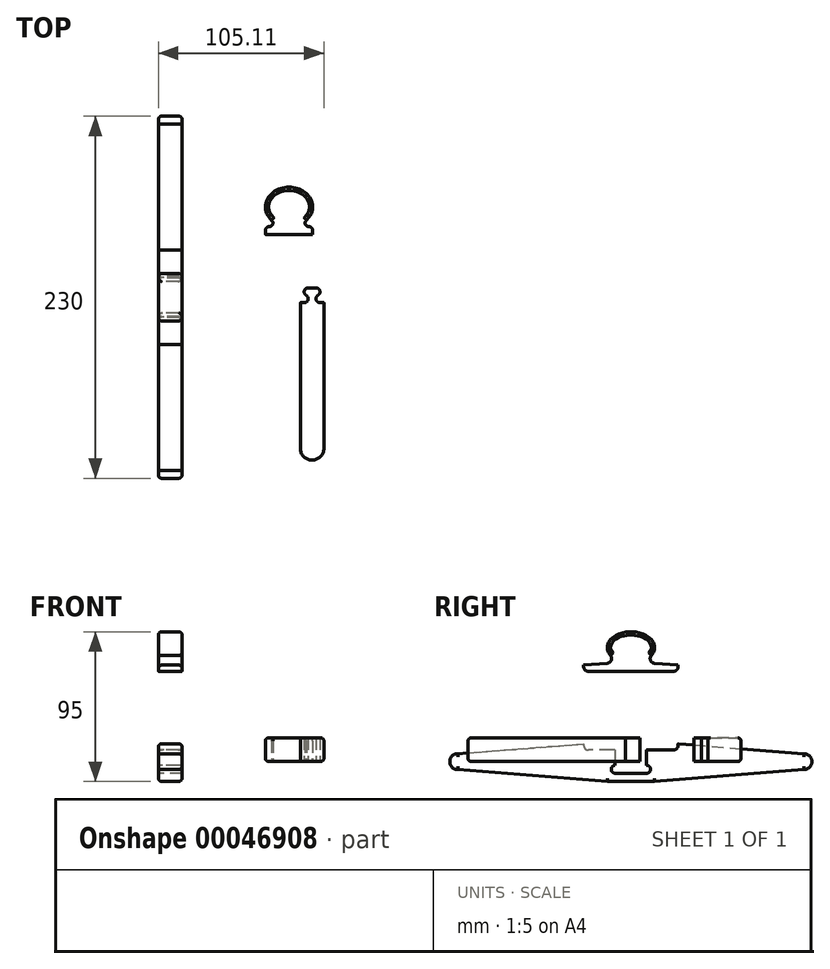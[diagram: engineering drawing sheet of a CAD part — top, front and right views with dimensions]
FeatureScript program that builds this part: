
annotation { "Feature Type Name" : "Feature", "Feature Type Description" : "" }
export const myFeature = defineFeature(function(context is Context, id is Id, definition is map)
    precondition{}
    {
        {
            var Q0;
            Q0=qCreatedBy(makeId("Right.planeOp"),FACE);
            var sketch = newSketch(context, id + "F0", { "sketchPlane" : qUnion([Q0])});
            skLineSegment(sketch, "E0.MirrorCS", {"start": v(-14.97, 12.4) * mm, "end": v(-109.97, 4.9) * mm, "construction": true});
            skLineSegment(sketch, "E1.rect.top", {"start": v(-9.97, -7.45) * mm, "end": v(10.03, -7.45) * mm});
            skLineSegment(sketch, "E2.rect.top", {"start": v(-14.97, -12.6) * mm, "end": v(15.03, -12.6) * mm});
            skLineSegment(sketch, "E1.rect.bottom", {"start": v(-9.97, 7.26) * mm, "end": v(10.03, 7.26) * mm});
            skLineSegment(sketch, "E3", {"start": v(0.03, 22.4) * mm, "end": v(-14.97, 22.4) * mm, "construction": true});
            skLineSegment(sketch, "E2.rect.right", {"start": v(15.03, 12.4) * mm, "end": v(15.03, -12.6) * mm, "construction": true});
            skLineSegment(sketch, "E1.rect.left", {"start": v(-9.97, 7.26) * mm, "end": v(-9.97, -2.45) * mm});
            skLineSegment(sketch, "E2.rect.left", {"start": v(-14.97, 12.4) * mm, "end": v(-14.97, -12.6) * mm, "construction": true});
            skLineSegment(sketch, "E4", {"start": v(15.03, -0.1) * mm, "end": v(115.03, -0.1) * mm, "construction": true});
            skLineSegment(sketch, "E5.MirrorCS", {"start": v(-14.97, -12.6) * mm, "end": v(-109.97, -5.1) * mm});
            skPoint(sketch, "E4.endSnap0", {"position": v(15.03, -0.1) * mm});
            skLineSegment(sketch, "E6.MirrorCS", {"start": v(15.03, 12.4) * mm, "end": v(110.03, 4.9) * mm, "construction": true});
            skLineSegment(sketch, "E7", {"start": v(15.03, -12.6) * mm, "end": v(110.03, -5.1) * mm});
            skEllipse(sketch, "E8", {"center": v(0.03, 22.4) * mm, "majorRadius": 10 * mm, "minorRadius": 15 * mm, "majorAxis": v(0, 1)});
            skLineSegment(sketch, "E1.rect.right", {"start": v(10.03, 7.26) * mm, "end": v(10.03, -2.45) * mm});
            skLineSegment(sketch, "E9", {"start": v(0.03, 12.4) * mm, "end": v(0.03, 32.4) * mm, "construction": true});
            skLineSegment(sketch, "E10", {"start": v(0.03, 12.4) * mm, "end": v(0.03, -12.6) * mm, "construction": true});
            skArc(sketch, "E11.MirrorCS", {"start": v(-114.97, -0.1) * mm, "mid": v(-113.5, 3.44) * mm, "end": v(-109.97, 4.9) * mm});
            skArc(sketch, "E12.MirrorCS", {"start": v(-114.97, -0.1) * mm, "mid": v(-113.5, -3.63) * mm, "end": v(-109.97, -5.1) * mm});
            skArc(sketch, "E13", {"start": v(115.03, -0.1) * mm, "mid": v(113.56, 3.44) * mm, "end": v(110.03, 4.9) * mm});
            skArc(sketch, "E14.MirrorCS", {"start": v(115.03, -0.1) * mm, "mid": v(113.56, -3.63) * mm, "end": v(110.03, -5.1) * mm});
            skLineSegment(sketch, "E15", {"start": v(115.03, -0.1) * mm, "end": v(110.03, -0.1) * mm, "construction": true});
            skLineSegment(sketch, "E16", {"start": v(30.03, 10.26) * mm, "end": v(30.03, 11.22) * mm, "construction": true});
            skLineSegment(sketch, "E17", {"start": v(0.03, 7.26) * mm, "end": v(27.03, 7.26) * mm, "construction": true});
            skArc(sketch, "E18.filletArc", {"start": v(27.03, 7.26) * mm, "mid": v(29.15, 8.14) * mm, "end": v(30.03, 10.26) * mm, "construction": true});
            skLineSegment(sketch, "E19", {"start": v(0.03, 7.26) * mm, "end": v(27.03, 7.26) * mm});
            skLineSegment(sketch, "E20", {"start": v(30.03, 10.26) * mm, "end": v(30.03, 11.22) * mm});
            skLineSegment(sketch, "E21", {"start": v(30.03, 11.22) * mm, "end": v(15.03, 12.4) * mm});
            skLineSegment(sketch, "E22", {"start": v(30.03, 11.22) * mm, "end": v(110.03, 4.9) * mm});
            skLineSegment(sketch, "E23.MirrorCS", {"start": v(0.03, 7.26) * mm, "end": v(-26.97, 7.26) * mm});
            skArc(sketch, "E24.MirrorCS", {"start": v(-26.97, 7.26) * mm, "mid": v(-29.1, 8.14) * mm, "end": v(-29.97, 10.26) * mm});
            skLineSegment(sketch, "E25.MirrorCS", {"start": v(-29.97, 10.26) * mm, "end": v(-29.97, 11.22) * mm});
            skLineSegment(sketch, "E26", {"start": v(-29.97, 11.22) * mm, "end": v(-14.97, 12.4) * mm});
            skArc(sketch, "E27", {"start": v(27.03, 7.26) * mm, "mid": v(29.15, 8.14) * mm, "end": v(30.03, 10.26) * mm});
            skLineSegment(sketch, "E28", {"start": v(-109.97, 4.9) * mm, "end": v(-29.97, 11.22) * mm});
            skLineSegment(sketch, "E29", {"start": v(0.03, 22.4) * mm, "end": v(0.03, 94.67) * mm, "construction": true});
            skLineSegment(sketch, "E30.direction1", {"start": v(0.03, 22.4) * mm, "end": v(26.12, 22.4) * mm, "construction": true});
            skLineSegment(sketch, "E31", {"start": v(0.03, 12.4) * mm, "end": v(0.03, 17.4) * mm, "construction": true});
            skLineSegment(sketch, "E32", {"start": v(0.03, 17.4) * mm, "end": v(-12.96, 17.4) * mm, "construction": true});
            skArc(sketch, "E33", {"start": v(-14.97, 12.4) * mm, "mid": v(-12.42, 14.28) * mm, "end": v(-12.96, 17.4) * mm});
            skArc(sketch, "E34.MirrorCS", {"start": v(15.03, 12.4) * mm, "mid": v(12.47, 14.28) * mm, "end": v(13.02, 17.4) * mm});
            skArc(sketch, "E35.0.1.1", {"start": v(15.03, 62.4) * mm, "mid": v(12.47, 64.28) * mm, "end": v(13.02, 67.4) * mm});
            skLineSegment(sketch, "E35.0.1.2", {"start": v(30.03, 61.22) * mm, "end": v(15.03, 62.4) * mm});
            skLineSegment(sketch, "E35.0.1.3", {"start": v(30.03, 60.26) * mm, "end": v(30.03, 61.22) * mm});
            skArc(sketch, "E35.0.1.4", {"start": v(27.03, 57.26) * mm, "mid": v(29.15, 58.14) * mm, "end": v(30.03, 60.26) * mm});
            skLineSegment(sketch, "E35.0.1.5", {"start": v(0.03, 57.26) * mm, "end": v(27.03, 57.26) * mm});
            skLineSegment(sketch, "E35.0.1.6", {"start": v(0.03, 57.26) * mm, "end": v(-26.97, 57.26) * mm});
            skArc(sketch, "E35.0.1.7", {"start": v(-26.97, 57.26) * mm, "mid": v(-29.1, 58.14) * mm, "end": v(-29.97, 60.26) * mm});
            skLineSegment(sketch, "E35.0.1.8", {"start": v(-29.97, 60.26) * mm, "end": v(-29.97, 61.22) * mm});
            skLineSegment(sketch, "E35.0.1.9", {"start": v(-29.97, 61.22) * mm, "end": v(-14.97, 62.4) * mm});
            skArc(sketch, "E35.0.1.10", {"start": v(-14.97, 62.4) * mm, "mid": v(-12.42, 64.28) * mm, "end": v(-12.96, 67.4) * mm});
            skLineSegment(sketch, "E35.direction1", {"start": v(0.03, 22.4) * mm, "end": v(39.38, 22.4) * mm, "construction": true});
            skLineSegment(sketch, "E35.direction2", {"start": v(0.03, 22.4) * mm, "end": v(0.03, 72.4) * mm, "construction": true});
            skEllipticalArc(sketch, "E36", {});
            skEllipticalArc(sketch, "E37", {"construction": true});
            skFitSpline(sketch, "E38.0", {"points": [v(-16.32, 73.6) * mm, v(-16.4, 72.4) * mm, v(-16.32, 71.21) * mm, v(-15.97, 69.65) * mm, v(-15.3, 68.17) * mm, v(-14.32, 66.8) * mm, v(-13.16, 65.52) * mm, v(-11.42, 64.11) * mm, v(-9.35, 62.98) * mm, v(-7.52, 62.25) * mm, v(-5.61, 61.65) * mm, v(-3.6, 61.24) * mm, v(-1.54, 61.04) * mm, v(0.03, 60.99) * mm, v(1.6, 61.04) * mm, v(3.66, 61.24) * mm, v(5.67, 61.65) * mm, v(7.57, 62.25) * mm, v(9.4, 62.98) * mm, v(11.48, 64.11) * mm, v(13.21, 65.52) * mm, v(14.37, 66.8) * mm, v(15.34, 68.17) * mm, v(16.02, 69.65) * mm, v(16.37, 71.21) * mm, v(16.46, 72.4) * mm, v(16.37, 73.6) * mm, v(16.02, 75.15) * mm, v(15.34, 76.63) * mm, v(14.37, 78) * mm, v(13.21, 79.29) * mm, v(11.48, 80.7) * mm, v(9.4, 81.83) * mm, v(7.57, 82.56) * mm, v(5.67, 83.16) * mm, v(3.66, 83.56) * mm, v(1.6, 83.77) * mm, v(0.03, 83.82) * mm, v(-1.54, 83.77) * mm, v(-3.6, 83.56) * mm, v(-5.61, 83.16) * mm, v(-7.52, 82.56) * mm, v(-9.35, 81.83) * mm, v(-11.42, 80.7) * mm, v(-13.16, 79.29) * mm, v(-14.32, 78) * mm, v(-15.3, 76.63) * mm, v(-15.97, 75.15) * mm, v(-16.32, 73.6) * mm, v(-16.4, 72.4) * mm, v(-16.32, 71.21) * mm], "construction": true});
            skArc(sketch, "E39.0", {"start": v(-15.08, 63.8) * mm, "mid": v(-13.72, 64.8) * mm, "end": v(-14, 66.47) * mm, "construction": true});
            skLineSegment(sketch, "E39.1", {"start": v(-31.37, 62.51) * mm, "end": v(-15.08, 63.8) * mm, "construction": true});
            skLineSegment(sketch, "E39.2", {"start": v(-31.37, 60.26) * mm, "end": v(-31.37, 62.51) * mm, "construction": true});
            skArc(sketch, "E39.3", {"start": v(-26.97, 55.86) * mm, "mid": v(-30.09, 57.15) * mm, "end": v(-31.37, 60.26) * mm, "construction": true});
            skLineSegment(sketch, "E39.4", {"start": v(0.04, 55.86) * mm, "end": v(-26.97, 55.86) * mm, "construction": true});
            skLineSegment(sketch, "E39.5", {"start": v(0.04, 55.86) * mm, "end": v(27.03, 55.86) * mm, "construction": true});
            skArc(sketch, "E39.6", {"start": v(15.14, 63.8) * mm, "mid": v(13.77, 64.8) * mm, "end": v(14.06, 66.47) * mm, "construction": true});
            skLineSegment(sketch, "E39.7", {"start": v(31.43, 62.51) * mm, "end": v(15.14, 63.8) * mm, "construction": true});
            skLineSegment(sketch, "E39.8", {"start": v(31.43, 60.26) * mm, "end": v(31.43, 62.51) * mm, "construction": true});
            skArc(sketch, "E39.9", {"start": v(27.03, 55.86) * mm, "mid": v(30.14, 57.15) * mm, "end": v(31.43, 60.26) * mm, "construction": true});
            skLineSegment(sketch, "E40.0", {"start": v(0.03, 8.85) * mm, "end": v(27.03, 8.85) * mm, "construction": true});
            skLineSegment(sketch, "E40.1", {"start": v(0.03, 8.85) * mm, "end": v(-26.97, 8.85) * mm, "construction": true});
            skArc(sketch, "E40.2", {"start": v(-26.97, 8.85) * mm, "mid": v(-27.97, 9.26) * mm, "end": v(-28.38, 10.26) * mm, "construction": true});
            skLineSegment(sketch, "E40.3", {"start": v(-28.38, 10.26) * mm, "end": v(-28.38, 12.95) * mm, "construction": true});
            skArc(sketch, "E40.4", {"start": v(116.62, -0.1) * mm, "mid": v(114.71, -4.74) * mm, "end": v(110.1, -6.7) * mm, "construction": true});
            skArc(sketch, "E40.5", {"start": v(116.62, -0.1) * mm, "mid": v(114.71, 4.54) * mm, "end": v(110.1, 6.5) * mm, "construction": true});
            skLineSegment(sketch, "E40.6", {"start": v(28.43, 12.95) * mm, "end": v(110.1, 6.5) * mm, "construction": true});
            skLineSegment(sketch, "E40.7", {"start": v(28.43, 10.26) * mm, "end": v(28.43, 12.95) * mm, "construction": true});
            skLineSegment(sketch, "E40.8", {"start": v(15.09, -14.2) * mm, "end": v(110.1, -6.7) * mm, "construction": true});
            skLineSegment(sketch, "E40.9", {"start": v(-15.04, -14.2) * mm, "end": v(15.09, -14.2) * mm, "construction": true});
            skLineSegment(sketch, "E40.10", {"start": v(-15.04, -14.2) * mm, "end": v(-110.04, -6.7) * mm, "construction": true});
            skArc(sketch, "E40.11", {"start": v(-116.57, -0.1) * mm, "mid": v(-114.66, -4.74) * mm, "end": v(-110.04, -6.7) * mm, "construction": true});
            skArc(sketch, "E40.12", {"start": v(27.03, 8.85) * mm, "mid": v(28.02, 9.26) * mm, "end": v(28.43, 10.26) * mm, "construction": true});
            skArc(sketch, "E40.13", {"start": v(-116.57, -0.1) * mm, "mid": v(-114.66, 4.54) * mm, "end": v(-110.04, 6.5) * mm, "construction": true});
            skLineSegment(sketch, "E40.14", {"start": v(-110.04, 6.5) * mm, "end": v(-28.38, 12.95) * mm, "construction": true});
            skLineSegment(sketch, "E41", {"start": v(-9.97, -7.45) * mm, "end": v(-9.97, -2.45) * mm, "construction": true});
            skArc(sketch, "E42", {"start": v(-9.97, -7.45) * mm, "mid": v(-12.47, -4.95) * mm, "end": v(-9.97, -2.45) * mm});
            skArc(sketch, "E43.MirrorCS", {"start": v(10.03, -7.45) * mm, "mid": v(12.53, -4.95) * mm, "end": v(10.03, -2.45) * mm});
            skLineSegment(sketch, "E44", {"start": v(10.03, -2.45) * mm, "end": v(10.03, -7.45) * mm, "construction": true});
            const initialGuessF0  = {"E36": [2.5925439463066354e-05, 0.07240322508186761, 0, 1, 0.01, 0.015, 4.188790204911169, 2.1000309035537947], "E37": [2.5925439463066354e-05, 0.07240322508186761, 0, 1, 0.01, 0.015, 2.1000309035537947, 4.188790204911169]};
            skSetInitialGuess(sketch, initialGuessF0);
            skSolve(sketch);
        }
        {
            var Q0;
            Q0=makeQuery(id+"F0.imprint","IMPRINT",FACE,{"disambiguationData":[TD([[makeQuery(id+"F0.imprint","IMPRINT",EDGE,{"derivedFrom":sQuery(id+"F0.wireOp",EDGE,"E1.rect.top")}),-1.0]])]});
            extrude(context, id + "F1", {"entities" : qUnion([Q0]), "depth" : 15 * mm});
        }
        {
            var Q0;
            {var subQ0=sQuery(id+"F0.wireOp",EDGE,"E35.0.1.10");var subQ1=sQuery(id+"F0.wireOp",EDGE,"E35.0.1.0");var subQ2=makeQuery(id+"F0.imprint","INTERSECT",VERTEX,{"disambiguationData":[OD(1.0)],"derivedFrom":[subQ1,subQ0]});Q0=makeQuery(id+"F0.imprint","IMPRINT",FACE,{"disambiguationData":[TD([[makeQuery(id+"F0.imprint","IMPRINT",EDGE,{"disambiguationData":[TD([[subQ2,-1.0]])],"derivedFrom":subQ1}),1.0]])]});}
            var Q1;
            {var subQ4=sQuery(id+"F0.wireOp",EDGE,"E35.0.1.2");Q1=makeQuery(id+"F0.imprint","IMPRINT",FACE,{"disambiguationData":[TD([[makeQuery(id+"F0.imprint","IMPRINT",EDGE,{"derivedFrom":subQ4}),1.0]])]});}
            extrude(context, id + "F2", {"entities" : qUnion([Q0, Q1]), "depth" : 15 * mm});
        }
        {
            var Q0;
            Q0=qCreatedBy(makeId("Top.planeOp"),FACE);
            var sketch = newSketch(context, id + "F3", { "sketchPlane" : qUnion([Q0])});
            skLineSegment(sketch, "E45", {"start": v(90.11, -3.41) * mm, "end": v(92.61, -3.41) * mm});
            skCircle(sketch, "E46", {"center": v(92.61, -0.91) * mm, "radius": 2.5 * mm, "construction": true});
            skArc(sketch, "E47", {"start": v(93.86, 1.25) * mm, "mid": v(95.03, -1.56) * mm, "end": v(92.61, -3.41) * mm});
            skLineSegment(sketch, "E48", {"start": v(92.61, -0.91) * mm, "end": v(95.11, 3.42) * mm, "construction": true});
            skArc(sketch, "E49", {"start": v(95.11, 5.92) * mm, "mid": v(92.7, 4.06) * mm, "end": v(93.86, 1.25) * mm});
            skCircle(sketch, "E50", {"center": v(95.11, 3.42) * mm, "radius": 2.5 * mm, "construction": true});
            skLineSegment(sketch, "E51", {"start": v(95.11, 3.42) * mm, "end": v(100.11, 3.42) * mm, "construction": true});
            skLineSegment(sketch, "E52", {"start": v(97.61, 3.42) * mm, "end": v(97.61, -0.91) * mm, "construction": true});
            skCircle(sketch, "E53", {"center": v(100.11, 3.42) * mm, "radius": 2.5 * mm, "construction": true});
            skLineSegment(sketch, "E54", {"start": v(95.11, 5.92) * mm, "end": v(100.11, 5.92) * mm});
            skArc(sketch, "E55", {"start": v(100.11, 5.92) * mm, "mid": v(102.53, 4.06) * mm, "end": v(101.36, 1.25) * mm});
            skArc(sketch, "E56", {"start": v(101.36, 1.25) * mm, "mid": v(100.2, -1.56) * mm, "end": v(102.61, -3.41) * mm});
            skCircle(sketch, "E57.MirrorC", {"center": v(102.61, -0.91) * mm, "radius": 2.5 * mm, "construction": true});
            skLineSegment(sketch, "E58.MirrorCS", {"start": v(102.61, -0.91) * mm, "end": v(97.61, -0.91) * mm, "construction": true});
            skLineSegment(sketch, "E59", {"start": v(92.61, -0.91) * mm, "end": v(97.61, -0.91) * mm, "construction": true});
            skLineSegment(sketch, "E60", {"start": v(105.11, -3.41) * mm, "end": v(102.61, -3.41) * mm});
            skLineSegment(sketch, "E61", {"start": v(92.61, -3.41) * mm, "end": v(105.11, -3.41) * mm, "construction": true});
            skLineSegment(sketch, "E62", {"start": v(100.11, 3.42) * mm, "end": v(102.61, 3.42) * mm, "construction": true});
            skLineSegment(sketch, "E63", {"start": v(95.11, 3.42) * mm, "end": v(92.61, 3.42) * mm, "construction": true});
            skLineSegment(sketch, "E64", {"start": v(97.61, -0.91) * mm, "end": v(97.61, -3.41) * mm, "construction": true});
            skLineSegment(sketch, "E65", {"start": v(97.61, -3.41) * mm, "end": v(97.61, -103.41) * mm, "construction": true});
            skLineSegment(sketch, "E66", {"start": v(97.61, -103.41) * mm, "end": v(97.61, -95.91) * mm, "construction": true});
            skLineSegment(sketch, "E67", {"start": v(105.11, -3.41) * mm, "end": v(97.61, -3.41) * mm, "construction": true});
            skArc(sketch, "E68", {"start": v(90.11, -95.91) * mm, "mid": v(97.61, -103.41) * mm, "end": v(105.11, -95.91) * mm});
            skLineSegment(sketch, "E69", {"start": v(90.11, -3.41) * mm, "end": v(90.11, -95.91) * mm});
            skLineSegment(sketch, "E70", {"start": v(105.11, -95.91) * mm, "end": v(105.11, -3.41) * mm});
            skPoint(sketch, "E71.firstSnap0", {"position": v(82.96, 44.92) * mm});
            skPoint(sketch, "E71.firstSnap1", {"position": v(97.96, 57.42) * mm});
            skPoint(sketch, "E71.oppositeSnap0", {"position": v(67.96, 57.42) * mm});
            skLineSegment(sketch, "E71.bottom", {"start": v(97.96, 44.92) * mm, "end": v(82.96, 44.92) * mm, "construction": true});
            skLineSegment(sketch, "E71.top", {"start": v(97.96, 39.92) * mm, "end": v(67.96, 39.92) * mm});
            skLineSegment(sketch, "E71.left", {"start": v(97.96, 44.92) * mm, "end": v(97.96, 39.92) * mm, "construction": true});
            skLineSegment(sketch, "E71.right", {"start": v(67.96, 42.42) * mm, "end": v(67.96, 39.92) * mm});
            skArc(sketch, "E72.filletArc", {"start": v(70.46, 44.92) * mm, "mid": v(68.7, 44.18) * mm, "end": v(67.96, 42.42) * mm});
            skLineSegment(sketch, "E73", {"start": v(82.96, 44.92) * mm, "end": v(82.96, 48.92) * mm, "construction": true});
            skLineSegment(sketch, "E74", {"start": v(82.96, 48.92) * mm, "end": v(71.96, 48.92) * mm, "construction": true});
            skArc(sketch, "E75", {"start": v(70.46, 44.92) * mm, "mid": v(72.6, 46.4) * mm, "end": v(71.96, 48.92) * mm});
            skArc(sketch, "E76.MirrorCS", {"start": v(95.46, 44.92) * mm, "mid": v(93.32, 46.4) * mm, "end": v(93.96, 48.92) * mm});
            skArc(sketch, "E77.MirrorCS", {"start": v(95.46, 44.92) * mm, "mid": v(97.23, 44.18) * mm, "end": v(97.96, 42.42) * mm});
            skEllipticalArc(sketch, "E78", {"construction": true});
            skEllipticalArc(sketch, "E79", {"construction": true});
            skEllipticalArc(sketch, "E80", {});
            skLineSegment(sketch, "E81", {"start": v(82.96, 44.92) * mm, "end": v(70.46, 44.92) * mm, "construction": true});
            skLineSegment(sketch, "E82", {"start": v(97.96, 39.92) * mm, "end": v(97.96, 42.42) * mm});
            const initialGuessF3  = {"E78": [0.08296047896146774, 0.05741671100258827, 1, 0, 0.015, 0.0125, 3.8893552882497127, 4.71238898038469], "E79": [0.08296047896146774, 0.05741671100258827, 1, 0, 0.015, 0.0125, 4.71238898038469, 5.535422672519729], "E80": [0.08296047896146774, 0.05741671100258827, 1, 0, 0.015, 0.0125, 5.535422672519729, 3.8932569177582783]};
            skSetInitialGuess(sketch, initialGuessF3);
            skSolve(sketch);
        }
        {
            var Q0;
            Q0 = qSketchRegion(id + "F3", true);
            var Q1;
            Q1=makeQuery(id+"F3.imprint","IMPRINT",FACE,{"disambiguationData":[TD([[makeQuery(id+"F3.imprint","IMPRINT",EDGE,{"derivedFrom":sQuery(id+"F3.wireOp",EDGE,"E45")}),-1.0]])]});
            extrude(context, id + "F4", {"entities" : qUnion([Q0, Q1]), "depth" : 15 * mm});
        }
        {
            var Q0;
            Q0=makeQuery(id+"F3.imprint","IMPRINT",FACE,{"disambiguationData":[TD([[makeQuery(id+"F3.imprint","IMPRINT",EDGE,{"derivedFrom":sQuery(id+"F3.wireOp",EDGE,"E71.top")}),-1.0]])]});
            extrude(context, id + "F5", {"entities" : qUnion([Q0]), "operationType" : NewBodyOperationType.ADD, "depth" : 15 * mm});
        }
        {
            var Q0;
            Q0=makeQuery(id+"F1.opExtrude","CAP_EDGE",EDGE,{"disambiguationData":[OSD([sQuery(id+"F0.wireOp",EDGE,"E1.rect.right")])],"isStart":true});
            var Q1;
            Q1=makeQuery(id+"F1.opExtrude","CAP_EDGE",EDGE,{"disambiguationData":[OSD([sQuery(id+"F0.wireOp",EDGE,"E1.rect.left")])],"isStart":true});
            var Q2;
            Q2=makeQuery(id+"F1.opExtrude","CAP_EDGE",EDGE,{"disambiguationData":[OSD([sQuery(id+"F0.wireOp",EDGE,"E1.rect.right")])],"isStart":false});
            var Q3;
            Q3=makeQuery(id+"F1.opExtrude","CAP_EDGE",EDGE,{"disambiguationData":[OSD([sQuery(id+"F0.wireOp",EDGE,"E1.rect.left")])],"isStart":false});
            fillet(context, id + "F6", {"entities" : qUnion([Q0, Q1, Q2, Q3]), "radius" : 2.5 * mm, "tangentPropagation" : true, "allowEdgeOverflow" : false});
        }
        {
            var Q0;
            Q0=makeQuery(id+"F1.opExtrude","CAP_EDGE",EDGE,{"disambiguationData":[OSD([sQuery(id+"F0.wireOp",EDGE,"E2.rect.top")])],"isStart":false});
            var Q1;
            Q1=makeQuery(id+"F1.opExtrude","CAP_EDGE",EDGE,{"disambiguationData":[OSD([sQuery(id+"F0.wireOp",EDGE,"E7")])],"isStart":false});
            var Q2;
            Q2=makeQuery(id+"F1.opExtrude","CAP_EDGE",EDGE,{"disambiguationData":[OSD([sQuery(id+"F0.wireOp",EDGE,"E22")])],"isStart":false});
            var Q3;
            Q3=makeQuery(id+"F1.opExtrude","CAP_EDGE",EDGE,{"disambiguationData":[OSD([sQuery(id+"F0.wireOp",EDGE,"E13"),sQuery(id+"F0.wireOp",EDGE,"E14.MirrorCS")])],"isStart":false});
            var Q4;
            Q4=makeQuery(id+"F1.opExtrude","CAP_EDGE",EDGE,{"disambiguationData":[OSD([sQuery(id+"F0.wireOp",EDGE,"E7")])],"isStart":true});
            var Q5;
            Q5=makeQuery(id+"F1.opExtrude","CAP_EDGE",EDGE,{"disambiguationData":[OSD([sQuery(id+"F0.wireOp",EDGE,"E13"),sQuery(id+"F0.wireOp",EDGE,"E14.MirrorCS")])],"isStart":true});
            var Q6;
            Q6=makeQuery(id+"F1.opExtrude","CAP_EDGE",EDGE,{"disambiguationData":[OSD([sQuery(id+"F0.wireOp",EDGE,"E2.rect.top")])],"isStart":true});
            var Q7;
            Q7=makeQuery(id+"F1.opExtrude","CAP_EDGE",EDGE,{"disambiguationData":[OSD([sQuery(id+"F0.wireOp",EDGE,"E5.MirrorCS")])],"isStart":true});
            var Q8;
            Q8=makeQuery(id+"F1.opExtrude","CAP_EDGE",EDGE,{"disambiguationData":[OSD([sQuery(id+"F0.wireOp",EDGE,"E5.MirrorCS")])],"isStart":false});
            var Q9;
            Q9=makeQuery(id+"F1.opExtrude","CAP_EDGE",EDGE,{"disambiguationData":[OSD([sQuery(id+"F0.wireOp",EDGE,"E28")])],"isStart":false});
            var Q10;
            Q10=makeQuery(id+"F1.opExtrude","CAP_EDGE",EDGE,{"disambiguationData":[OSD([sQuery(id+"F0.wireOp",EDGE,"E11.MirrorCS"),sQuery(id+"F0.wireOp",EDGE,"E12.MirrorCS")])],"isStart":false});
            var Q11;
            Q11=makeQuery(id+"F1.opExtrude","CAP_EDGE",EDGE,{"disambiguationData":[OSD([sQuery(id+"F0.wireOp",EDGE,"E11.MirrorCS"),sQuery(id+"F0.wireOp",EDGE,"E12.MirrorCS")])],"isStart":true});
            var Q12;
            Q12=makeQuery(id+"F1.opExtrude","CAP_EDGE",EDGE,{"disambiguationData":[OSD([sQuery(id+"F0.wireOp",EDGE,"E28")])],"isStart":true});
            var Q13;
            Q13=makeQuery(id+"F1.opExtrude","CAP_EDGE",EDGE,{"disambiguationData":[OSD([sQuery(id+"F0.wireOp",EDGE,"E22")])],"isStart":true});
            fillet(context, id + "F7", {"entities" : qUnion([Q0, Q1, Q2, Q3, Q4, Q5, Q6, Q7, Q8, Q9, Q10, Q11, Q12, Q13]), "radius" : 2 * mm, "tangentPropagation" : true, "allowEdgeOverflow" : false});
        }
        {
            var Q0;
            Q0=makeQuery(id+"F2.opExtrude","CAP_EDGE",EDGE,{"disambiguationData":[OSD([sQuery(id+"F0.wireOp",EDGE,"E35.0.1.9")])],"isStart":true});
            var Q1;
            Q1=makeQuery(id+"F2.opExtrude","CAP_EDGE",EDGE,{"disambiguationData":[OSD([sQuery(id+"F0.wireOp",EDGE,"E36")])],"isStart":true});
            var Q2;
            Q2=makeQuery(id+"F2.opExtrude","CAP_EDGE",EDGE,{"disambiguationData":[OSD([sQuery(id+"F0.wireOp",EDGE,"E35.0.1.10")])],"isStart":true});
            var Q3;
            Q3=makeQuery(id+"F2.opExtrude","CAP_EDGE",EDGE,{"disambiguationData":[OSD([sQuery(id+"F0.wireOp",EDGE,"E35.0.1.1")])],"isStart":true});
            var Q4;
            Q4=makeQuery(id+"F2.opExtrude","CAP_EDGE",EDGE,{"disambiguationData":[OSD([sQuery(id+"F0.wireOp",EDGE,"E35.0.1.2")])],"isStart":true});
            var Q5;
            Q5=makeQuery(id+"F2.opExtrude","CAP_EDGE",EDGE,{"disambiguationData":[OSD([sQuery(id+"F0.wireOp",EDGE,"E35.0.1.2")])],"isStart":false});
            var Q6;
            Q6=makeQuery(id+"F2.opExtrude","CAP_EDGE",EDGE,{"disambiguationData":[OSD([sQuery(id+"F0.wireOp",EDGE,"E36")])],"isStart":false});
            var Q7;
            Q7=makeQuery(id+"F2.opExtrude","CAP_EDGE",EDGE,{"disambiguationData":[OSD([sQuery(id+"F0.wireOp",EDGE,"E35.0.1.10")])],"isStart":false});
            var Q8;
            Q8=makeQuery(id+"F2.opExtrude","CAP_EDGE",EDGE,{"disambiguationData":[OSD([sQuery(id+"F0.wireOp",EDGE,"E35.0.1.9")])],"isStart":false});
            fillet(context, id + "F8", {"entities" : qUnion([Q0, Q1, Q2, Q3, Q4, Q5, Q6, Q7, Q8]), "radius" : 2 * mm, "tangentPropagation" : true, "allowEdgeOverflow" : false});
        }
        {
            var Q0;
            Q0=makeQuery(id+"F4.opExtrude","CAP_EDGE",EDGE,{"disambiguationData":[OSD([sQuery(id+"F3.wireOp",EDGE,"E70")])],"isStart":false});
            var Q1;
            Q1=makeQuery(id+"F4.opExtrude","CAP_EDGE",EDGE,{"disambiguationData":[OSD([sQuery(id+"F3.wireOp",EDGE,"E70")])],"isStart":true});
            fillet(context, id + "F9", {"entities" : qUnion([Q0, Q1]), "radius" : 2 * mm, "tangentPropagation" : true, "allowEdgeOverflow" : false});
        }
        {
            var Q0;
            Q0=makeQuery(id+"F4.opExtrude","CAP_EDGE",EDGE,{"disambiguationData":[OSD([sQuery(id+"F3.wireOp",EDGE,"E80")])],"isStart":false});
            var Q1;
            Q1=makeQuery(id+"F4.opExtrude","CAP_EDGE",EDGE,{"disambiguationData":[OSD([sQuery(id+"F3.wireOp",EDGE,"E76.MirrorCS")])],"isStart":false});
            var Q2;
            Q2=makeQuery(id+"F4.opExtrude","CAP_EDGE",EDGE,{"disambiguationData":[OSD([sQuery(id+"F3.wireOp",EDGE,"E77.MirrorCS")])],"isStart":false});
            var Q3;
            Q3=makeQuery(id+"F4.opExtrude","CAP_EDGE",EDGE,{"disambiguationData":[OSD([sQuery(id+"F3.wireOp",EDGE,"E82")])],"isStart":false});
            var Q4;
            Q4=makeQuery(id+"F4.opExtrude","CAP_EDGE",EDGE,{"disambiguationData":[OSD([sQuery(id+"F3.wireOp",EDGE,"E75")])],"isStart":false});
            var Q5;
            Q5=makeQuery(id+"F4.opExtrude","CAP_EDGE",EDGE,{"disambiguationData":[OSD([sQuery(id+"F3.wireOp",EDGE,"E72.filletArc")])],"isStart":false});
            var Q6;
            Q6=makeQuery(id+"F4.opExtrude","CAP_EDGE",EDGE,{"disambiguationData":[OSD([sQuery(id+"F3.wireOp",EDGE,"E82")])],"isStart":true});
            var Q7;
            Q7=makeQuery(id+"F4.opExtrude","CAP_EDGE",EDGE,{"disambiguationData":[OSD([sQuery(id+"F3.wireOp",EDGE,"E77.MirrorCS")])],"isStart":true});
            var Q8;
            Q8=makeQuery(id+"F4.opExtrude","CAP_EDGE",EDGE,{"disambiguationData":[OSD([sQuery(id+"F3.wireOp",EDGE,"E80")])],"isStart":true});
            var Q9;
            Q9=makeQuery(id+"F4.opExtrude","CAP_EDGE",EDGE,{"disambiguationData":[OSD([sQuery(id+"F3.wireOp",EDGE,"E71.right")])],"isStart":true});
            fillet(context, id + "F10", {"entities" : qUnion([Q0, Q1, Q2, Q3, Q4, Q5, Q6, Q7, Q8, Q9]), "radius" : 2 * mm, "tangentPropagation" : true, "allowEdgeOverflow" : false});
        }
    });
